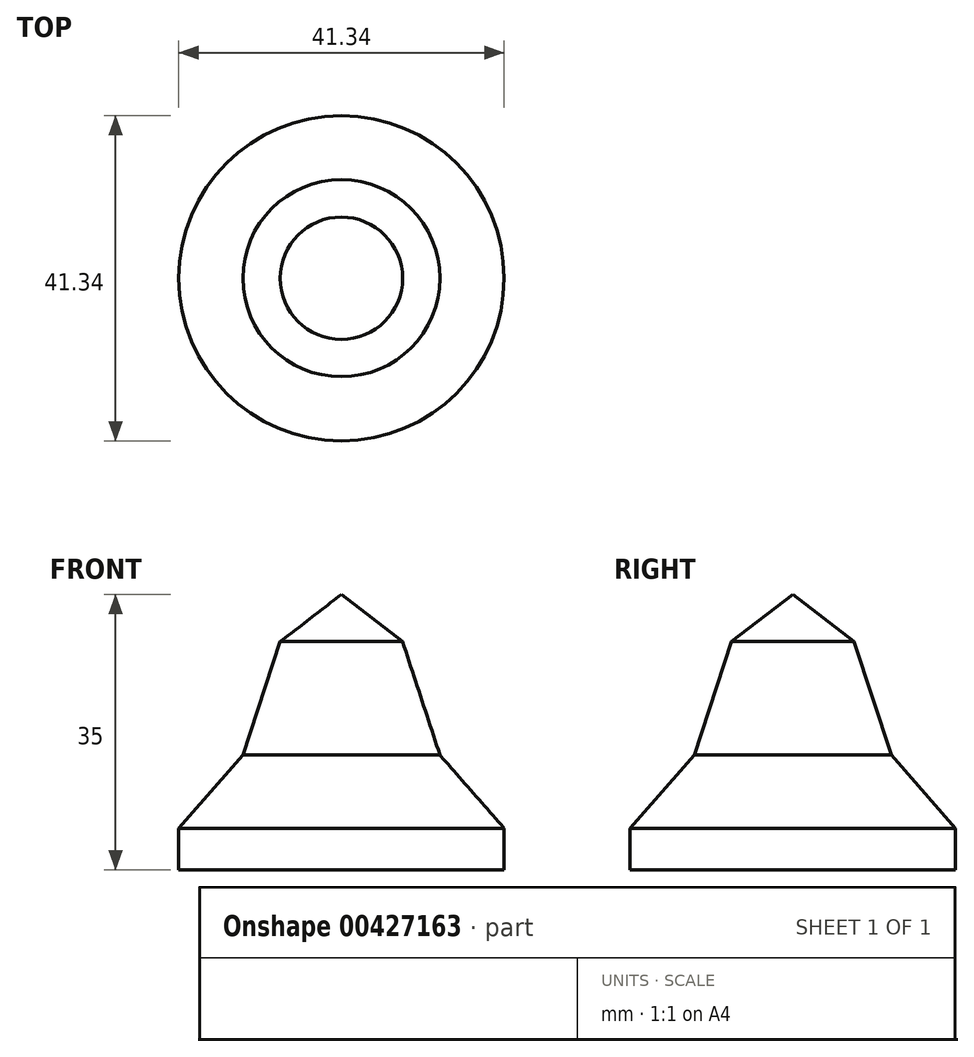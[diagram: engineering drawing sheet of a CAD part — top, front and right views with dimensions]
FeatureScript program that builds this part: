
annotation { "Feature Type Name" : "Feature", "Feature Type Description" : "" }
export const myFeature = defineFeature(function(context is Context, id is Id, definition is map)
    precondition{}
    {
        {
            var Q0;
            Q0=qCreatedBy(makeId("Front.planeOp"),FACE);
            var sketch = newSketch(context, id + "F0", { "sketchPlane" : qUnion([Q0])});
            skLineSegment(sketch, "E0", {"start": v(0, 0) * mm, "end": v(-20.67, 0) * mm});
            skLineSegment(sketch, "E1", {"start": v(-20.67, 0) * mm, "end": v(-20.67, 5.3) * mm});
            skLineSegment(sketch, "E2", {"start": v(-20.67, 5.3) * mm, "end": v(-12.51, 14.6) * mm});
            skLineSegment(sketch, "E3", {"start": v(-12.51, 14.6) * mm, "end": v(-7.77, 29) * mm});
            skLineSegment(sketch, "E4", {"start": v(-7.77, 29) * mm, "end": v(0, 35) * mm});
            skLineSegment(sketch, "E5", {"start": v(0, 35) * mm, "end": v(0, 0) * mm});
            skSolve(sketch);
        }
        {
            var Q0;
            Q0 = qSketchRegion(id + "F0", true);
            var Q1;
            Q1=sQuery(id+"F0.wireOp",EDGE,"E5");
            revolve(context, id + "F1", {"entities" : qUnion([Q0]), "axis" : qUnion([Q1]), "revolveType" : RevolveType.FULL});
        }
    });
